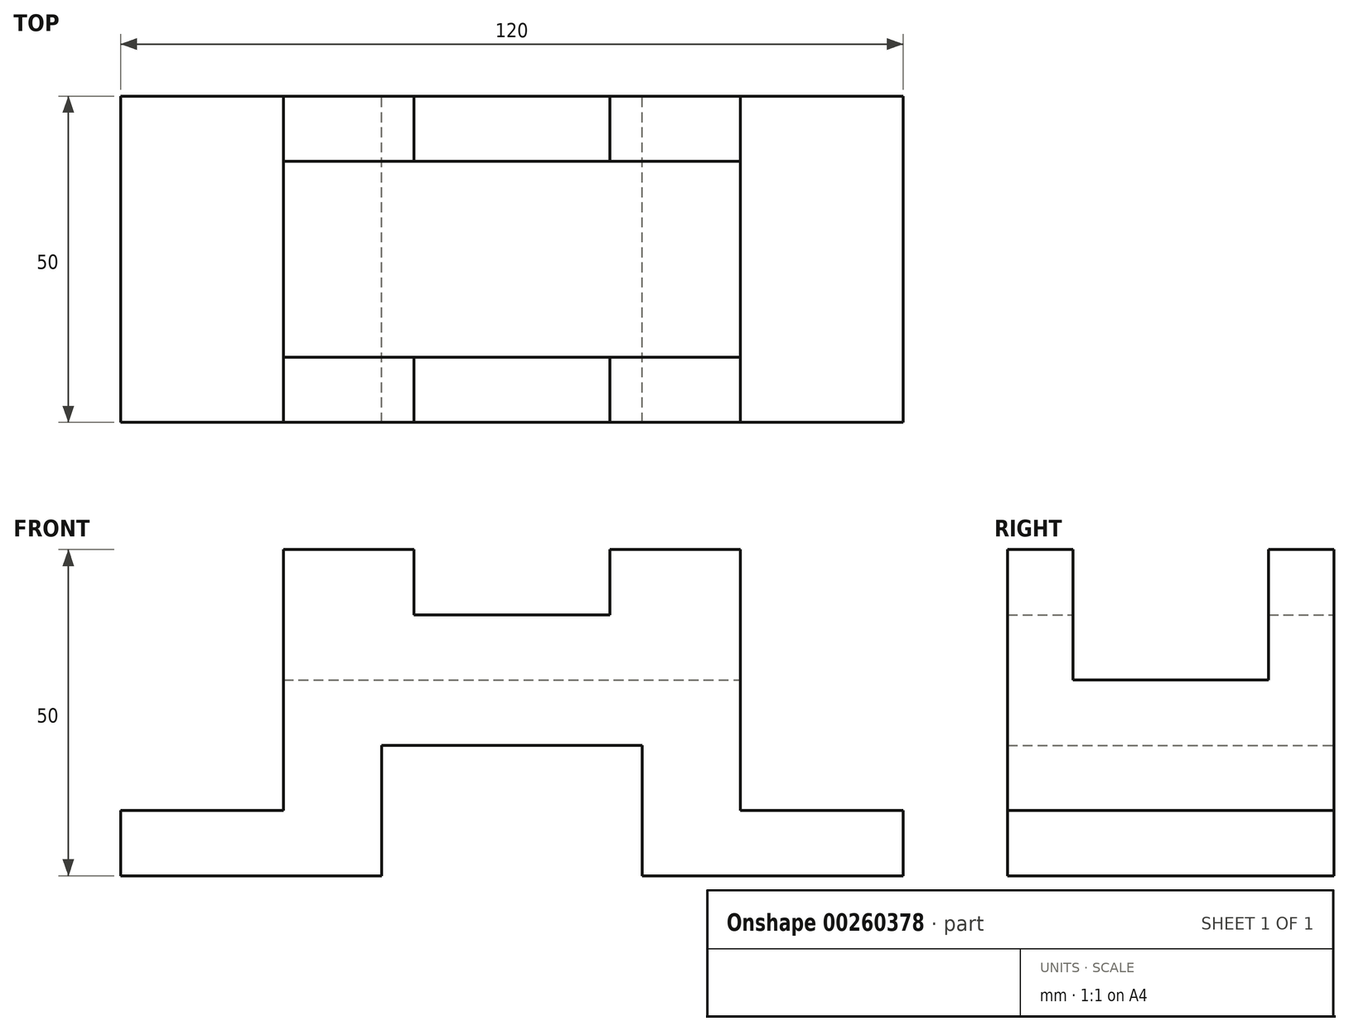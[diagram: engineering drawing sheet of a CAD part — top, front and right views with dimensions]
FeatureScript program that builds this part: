
annotation { "Feature Type Name" : "Feature", "Feature Type Description" : "" }
export const myFeature = defineFeature(function(context is Context, id is Id, definition is map)
    precondition{}
    {
        {
            var Q0;
            Q0=qCreatedBy(makeId("Front.planeOp"),FACE);
            var sketch = newSketch(context, id + "F0", { "sketchPlane" : qUnion([Q0])});
            skLineSegment(sketch, "E0", {"start": v(-20, 0) * mm, "end": v(-60, 0) * mm});
            skLineSegment(sketch, "E1", {"start": v(-60, 10) * mm, "end": v(-35, 10) * mm});
            skLineSegment(sketch, "E2", {"start": v(-60, 10) * mm, "end": v(-60, 0) * mm});
            skLineSegment(sketch, "E3", {"start": v(-35, 10) * mm, "end": v(-35, 50) * mm});
            skLineSegment(sketch, "E4", {"start": v(-35, 50) * mm, "end": v(-15, 50) * mm});
            skLineSegment(sketch, "E5", {"start": v(-15, 50) * mm, "end": v(-15, 40) * mm});
            skLineSegment(sketch, "E6", {"start": v(-15, 40) * mm, "end": v(0, 40) * mm});
            skLineSegment(sketch, "E7", {"start": v(0, 20) * mm, "end": v(-20, 20) * mm});
            skLineSegment(sketch, "E8", {"start": v(-20, 0) * mm, "end": v(-20, 0) * mm});
            skLineSegment(sketch, "E9", {"start": v(0, 40) * mm, "end": v(0, 20) * mm});
            skLineSegment(sketch, "E10", {"start": v(-20, 20) * mm, "end": v(-20, 0) * mm});
            skLineSegment(sketch, "E11.MirrorCS", {"start": v(35, 50) * mm, "end": v(15, 50) * mm});
            skLineSegment(sketch, "E12.MirrorCS", {"start": v(15, 40) * mm, "end": v(0, 40) * mm});
            skLineSegment(sketch, "E13.MirrorCS", {"start": v(0, 20) * mm, "end": v(20, 20) * mm});
            skLineSegment(sketch, "E14.MirrorCS", {"start": v(20, 20) * mm, "end": v(20, 0) * mm});
            skLineSegment(sketch, "E15.MirrorCS", {"start": v(20, 0) * mm, "end": v(60, 0) * mm});
            skLineSegment(sketch, "E16.MirrorCS", {"start": v(60, 10) * mm, "end": v(60, 0) * mm});
            skLineSegment(sketch, "E17.MirrorCS", {"start": v(60, 10) * mm, "end": v(35, 10) * mm});
            skLineSegment(sketch, "E18.MirrorCS", {"start": v(35, 10) * mm, "end": v(35, 50) * mm});
            skLineSegment(sketch, "E19.MirrorCS", {"start": v(15, 50) * mm, "end": v(15, 40) * mm});
            skSolve(sketch);
        }
        {
            var Q0;
            Q0=makeQuery(id+"F0.imprint","IMPRINT",FACE,{"disambiguationData":[TD([[makeQuery(id+"F0.imprint","IMPRINT",EDGE,{"derivedFrom":sQuery(id+"F0.wireOp",EDGE,"E0")}),-1.0]])]});
            var Q1;
            Q1=makeQuery(id+"F0.imprint","IMPRINT",FACE,{"disambiguationData":[TD([[makeQuery(id+"F0.imprint","IMPRINT",EDGE,{"derivedFrom":sQuery(id+"F0.wireOp",EDGE,"E9")}),1.0]])]});
            extrude(context, id + "F1", {"entities" : qUnion([Q0, Q1]), "depth" : 50 * mm});
        }
        {
            var Q0;
            Q0=makeQuery(id+"F1.opExtrude","SWEPT_FACE",FACE,{"disambiguationData":[OSD([sQuery(id+"F0.wireOp",EDGE,"E4")])]});
            var sketch = newSketch(context, id + "F2", { "sketchPlane" : qUnion([Q0])});
            skLineSegment(sketch, "E20.bottom", {"start": v(-35, -10) * mm, "end": v(35, -10) * mm});
            skLineSegment(sketch, "E20.top", {"start": v(-35, -40) * mm, "end": v(35, -40) * mm});
            skLineSegment(sketch, "E20.left", {"start": v(-35, -10) * mm, "end": v(-35, -40) * mm});
            skLineSegment(sketch, "E20.right", {"start": v(35, -10) * mm, "end": v(35, -40) * mm});
            skSolve(sketch);
        }
        {
            var Q0;
            {var subQ0=sQuery(id+"F2.wireOp",EDGE,"E20.left");Q0=makeQuery(id+"F2.imprint","IMPRINT",FACE,{"disambiguationData":[TD([[makeQuery(id+"F2.imprint","IMPRINT",EDGE,{"derivedFrom":subQ0}),-1.0]])]});}
            var Q1;
            {var subQ0=sQuery(id+"F2.wireOp",EDGE,"E20.right");Q1=makeQuery(id+"F2.imprint","IMPRINT",FACE,{"disambiguationData":[TD([[makeQuery(id+"F2.imprint","IMPRINT",EDGE,{"derivedFrom":subQ0}),-1.0]])]});}
            extrude(context, id + "F3", {"entities" : qUnion([Q0, Q1]), "operationType" : NewBodyOperationType.REMOVE, "oppositeDirection" : true, "depth" : 20 * mm});
        }
    });
